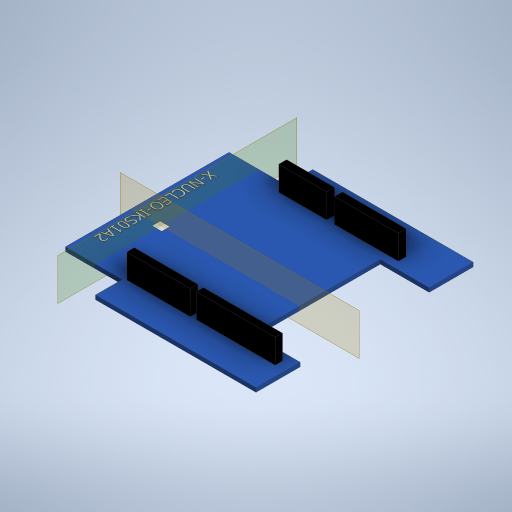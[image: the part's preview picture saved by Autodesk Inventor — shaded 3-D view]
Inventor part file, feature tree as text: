
AUTODESK INVENTOR PART (.ipt)
format: ipt  version: 2023 (Build 270158000, 158)  size: 787,968 bytes
history: native  units: mm
features: extrude x5, projected_geometry x4, sketch x3, other x3
ambient origin geometry x8: Origin, YZ Plane, XZ Plane, XY Plane, X Axis, Y Axis, Z Axis, Center Point
bodies: Body1 (feature_tree)
feature tree (15):
  sketch  "Esquisse1"
  extrude  "Extrusion2"  Depth=1.3mm TaperAngle=0.0deg
  extrude  "Extrusion3"  Depth=9.0mm TaperAngle=0.0deg
  extrude  "Extrusion4"  Depth=1.3001mm TaperAngle=0.0deg
  extrude  "Extrusion5"  Depth=1.0mm
  extrude  "Extrusion6"  Depth=1.294mm
  other  "Plan de construction1"
  other  "Plan de construction2"
  other  "Image1"
  sketch  "Esquisse2"
  projected_geometry  "Boucle projetée1"
  projected_geometry  "Boucle projetée2"
  projected_geometry  "Boucle projetée3"
  projected_geometry  "Boucle projetée4"
  sketch  "Esquisse3"
